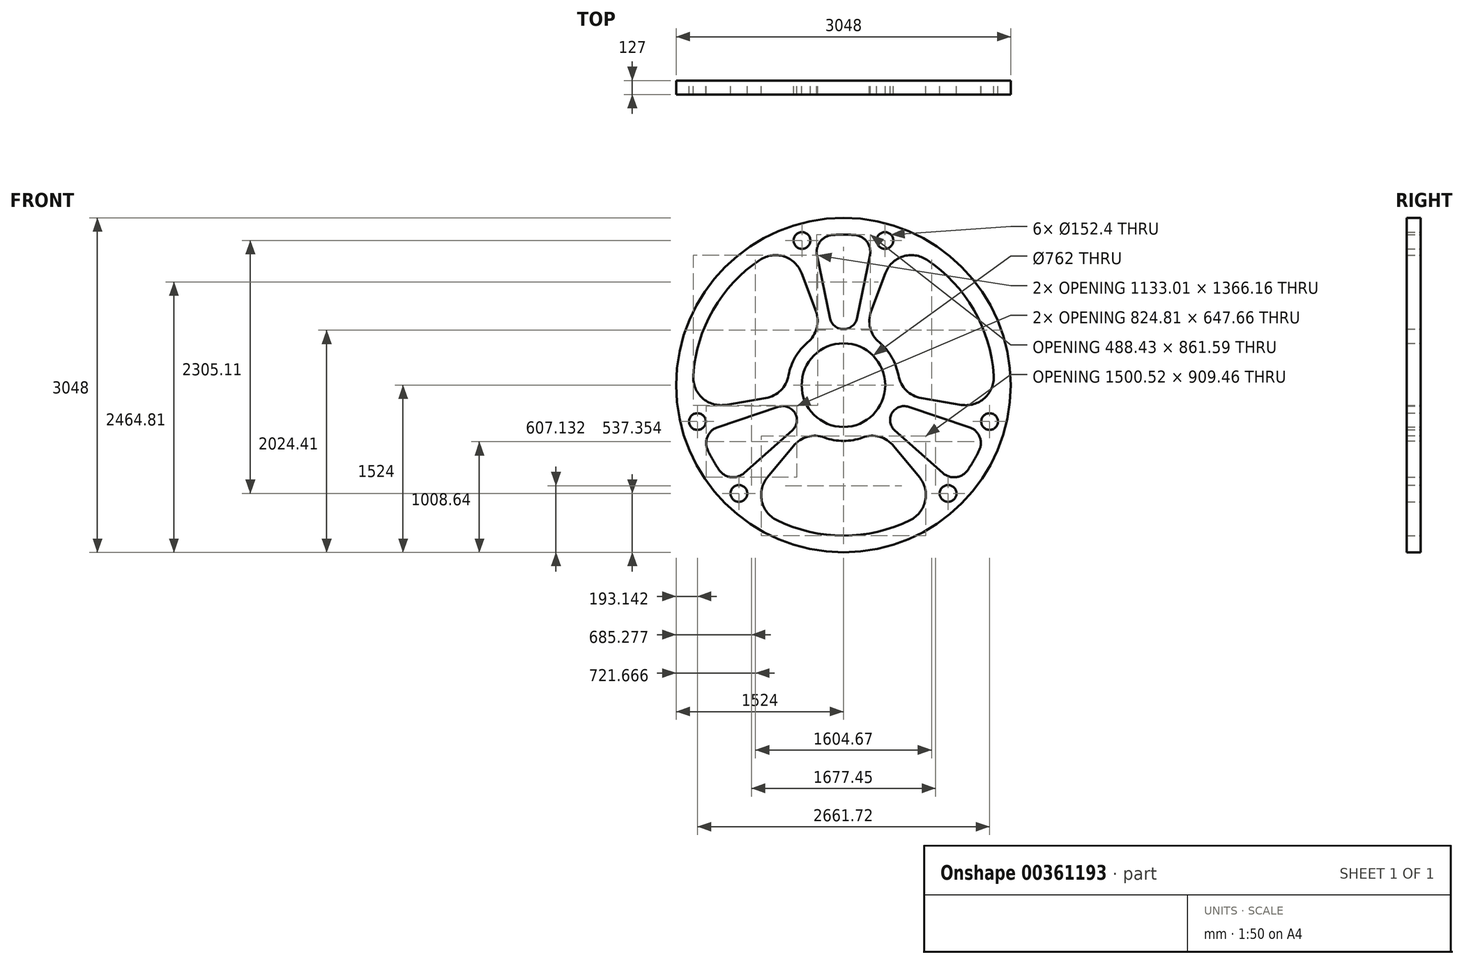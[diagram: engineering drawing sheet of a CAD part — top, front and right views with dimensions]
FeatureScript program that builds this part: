
annotation { "Feature Type Name" : "Feature", "Feature Type Description" : "" }
export const myFeature = defineFeature(function(context is Context, id is Id, definition is map)
    precondition{}
    {
        {
            var Q0;
            Q0=qCreatedBy(makeId("Front.planeOp"),FACE);
            var sketch = newSketch(context, id + "F0", { "sketchPlane" : qUnion([Q0])});
            skCircle(sketch, "E0", {"center": v(0, 0) * mm, "radius": 1524 * mm});
            skLineSegment(sketch, "E1", {"start": v(-124.45, 611.7) * mm, "end": v(-241.16, 1185.35) * mm});
            skLineSegment(sketch, "E2", {"start": v(124.45, 611.7) * mm, "end": v(241.16, 1185.35) * mm});
            skArc(sketch, "E3", {"start": v(-103.3, 1367.7) * mm, "mid": v(-213.39, 1307.65) * mm, "end": v(-241.16, 1185.35) * mm});
            skArc(sketch, "E4", {"start": v(241.16, 1185.35) * mm, "mid": v(213.39, 1307.65) * mm, "end": v(103.3, 1367.7) * mm});
            skArc(sketch, "E5.trimOffspring", {"start": v(103.3, 1367.7) * mm, "mid": v(0, 1371.6) * mm, "end": v(-103.3, 1367.7) * mm});
            skArc(sketch, "E6", {"start": v(-124.45, 611.7) * mm, "mid": v(0, 510.01) * mm, "end": v(124.45, 611.7) * mm});
            skLineSegment(sketch, "E7", {"start": v(0, 508) * mm, "end": v(0, 510.01) * mm});
            skCircle(sketch, "E8", {"center": v(-378.06, 1318.47) * mm, "radius": 76.2 * mm});
            skCircle(sketch, "E9", {"center": v(378.06, 1318.47) * mm, "radius": 76.2 * mm});
            skPoint(sketch, "E10.endSnap0", {"position": v(0, -1371.6) * mm});
            skLineSegment(sketch, "E11", {"start": v(-456.97, -554.35) * mm, "end": v(-692.28, -839.8) * mm});
            skArc(sketch, "E12", {"start": v(-326.34, 389.31) * mm, "mid": v(-439.94, 254) * mm, "end": v(-500.33, 87.96) * mm});
            skArc(sketch, "E13", {"start": v(-692.28, -839.8) * mm, "mid": v(-744.67, -1054.47) * mm, "end": v(-609.08, -1228.95) * mm});
            skArc(sketch, "E14", {"start": v(456.97, -554.35) * mm, "mid": v(327.73, -470.84) * mm, "end": v(173.99, -477.28) * mm});
            skArc(sketch, "E15", {"start": v(-173.99, -477.28) * mm, "mid": v(-327.73, -470.84) * mm, "end": v(-456.97, -554.35) * mm});
            skArc(sketch, "E16.trimOffspring", {"start": v(-609.08, -1228.95) * mm, "mid": v(0, -1371.6) * mm, "end": v(609.08, -1228.95) * mm});
            skPoint(sketch, "E17.orphan", {"position": v(0, -1524) * mm});
            skArc(sketch, "E18", {"start": v(609.08, -1228.95) * mm, "mid": v(744.67, -1054.47) * mm, "end": v(692.28, -839.8) * mm});
            skLineSegment(sketch, "E19.trimOffspring", {"start": v(456.97, -554.35) * mm, "end": v(692.28, -839.8) * mm});
            skCircle(sketch, "E20", {"center": v(0, 0) * mm, "radius": 381 * mm});
            skArc(sketch, "E21", {"start": v(-759.76, 1141.95) * mm, "mid": v(-1187.84, 685.8) * mm, "end": v(-1368.84, 87) * mm});
            skCircle(sketch, "E22.1.0", {"center": v(-1330.86, -331.82) * mm, "radius": 76.2 * mm});
            skCircle(sketch, "E22.1.1", {"center": v(-952.8, -986.65) * mm, "radius": 76.2 * mm});
            skLineSegment(sketch, "E22.1.2", {"start": v(-591.97, -198.07) * mm, "end": v(-1147.13, -383.82) * mm});
            skArc(sketch, "E22.1.3", {"start": v(-1147.13, -383.82) * mm, "mid": v(-1239.15, -469.02) * mm, "end": v(-1236.12, -594.4) * mm});
            skArc(sketch, "E22.1.4", {"start": v(-1132.82, -773.31) * mm, "mid": v(-1025.76, -838.62) * mm, "end": v(-905.96, -801.53) * mm});
            skLineSegment(sketch, "E22.1.5", {"start": v(-467.52, -413.62) * mm, "end": v(-905.96, -801.53) * mm});
            skArc(sketch, "E22.1.6", {"start": v(-467.52, -413.62) * mm, "mid": v(-441.68, -255) * mm, "end": v(-591.97, -198.07) * mm});
            skCircle(sketch, "E22.2.0", {"center": v(952.8, -986.65) * mm, "radius": 76.2 * mm});
            skCircle(sketch, "E22.2.1", {"center": v(1330.86, -331.82) * mm, "radius": 76.2 * mm});
            skLineSegment(sketch, "E22.2.2", {"start": v(467.52, -413.62) * mm, "end": v(905.96, -801.53) * mm});
            skArc(sketch, "E22.2.3", {"start": v(905.96, -801.53) * mm, "mid": v(1025.76, -838.62) * mm, "end": v(1132.82, -773.31) * mm});
            skArc(sketch, "E22.2.4", {"start": v(1236.12, -594.4) * mm, "mid": v(1239.15, -469.02) * mm, "end": v(1147.13, -383.82) * mm});
            skLineSegment(sketch, "E22.2.5", {"start": v(591.97, -198.07) * mm, "end": v(1147.13, -383.82) * mm});
            skArc(sketch, "E22.2.6", {"start": v(591.97, -198.07) * mm, "mid": v(441.68, -255) * mm, "end": v(467.52, -413.62) * mm});
            skArc(sketch, "E23.1.0", {"start": v(500.33, 87.96) * mm, "mid": v(571.62, -48.4) * mm, "end": v(708.57, -118.57) * mm});
            skLineSegment(sketch, "E23.1.1", {"start": v(708.57, -118.57) * mm, "end": v(1073.43, -179.63) * mm});
            skArc(sketch, "E23.1.2", {"start": v(1073.43, -179.63) * mm, "mid": v(1285.53, -117.67) * mm, "end": v(1368.84, 87) * mm});
            skLineSegment(sketch, "E23.1.4", {"start": v(251.6, 672.92) * mm, "end": v(381.15, 1019.43) * mm});
            skArc(sketch, "E23.1.5", {"start": v(251.6, 672.92) * mm, "mid": v(243.9, 519.24) * mm, "end": v(326.34, 389.31) * mm});
            skArc(sketch, "E23.1.6", {"start": v(759.76, 1141.95) * mm, "mid": v(540.86, 1172.14) * mm, "end": v(381.15, 1019.43) * mm});
            skArc(sketch, "E23.2.0", {"start": v(-326.34, 389.31) * mm, "mid": v(-243.9, 519.24) * mm, "end": v(-251.6, 672.92) * mm});
            skLineSegment(sketch, "E23.2.1", {"start": v(-251.6, 672.92) * mm, "end": v(-381.15, 1019.43) * mm});
            skArc(sketch, "E23.2.2", {"start": v(-381.15, 1019.43) * mm, "mid": v(-540.86, 1172.14) * mm, "end": v(-759.76, 1141.95) * mm});
            skLineSegment(sketch, "E23.2.4", {"start": v(-708.57, -118.57) * mm, "end": v(-1073.43, -179.63) * mm});
            skArc(sketch, "E23.2.5", {"start": v(-708.57, -118.57) * mm, "mid": v(-571.62, -48.4) * mm, "end": v(-500.33, 87.96) * mm});
            skArc(sketch, "E23.2.6", {"start": v(-1368.84, 87) * mm, "mid": v(-1285.53, -117.67) * mm, "end": v(-1073.43, -179.63) * mm});
            skArc(sketch, "E24.trimOffspring", {"start": v(-173.99, -477.28) * mm, "mid": v(0, -508) * mm, "end": v(173.99, -477.28) * mm});
            skArc(sketch, "E25.trimOffspring", {"start": v(500.33, 87.96) * mm, "mid": v(439.94, 254) * mm, "end": v(326.34, 389.31) * mm});
            skArc(sketch, "E26.trimOffspring", {"start": v(1132.82, -773.31) * mm, "mid": v(1187.84, -685.8) * mm, "end": v(1236.12, -594.4) * mm});
            skArc(sketch, "E27.trimOffspring", {"start": v(-609.08, -1228.95) * mm, "mid": v(-312.78, -1335.46) * mm, "end": v(0, -1371.6) * mm});
            skArc(sketch, "E28.trimOffspring", {"start": v(-1236.12, -594.4) * mm, "mid": v(-1187.84, -685.8) * mm, "end": v(-1132.82, -773.31) * mm});
            skArc(sketch, "E29.trimOffspring", {"start": v(1368.84, 87) * mm, "mid": v(1187.84, 685.8) * mm, "end": v(759.76, 1141.95) * mm});
            skCircle(sketch, "E30", {"center": v(0, 0) * mm, "radius": 127 * mm});
            skCircle(sketch, "E31", {"center": v(0, 254.8) * mm, "radius": 50.8 * mm});
            skCircle(sketch, "E32.1.0", {"center": v(220.67, -127.4) * mm, "radius": 50.8 * mm});
            skCircle(sketch, "E32.2.0", {"center": v(-220.67, -127.4) * mm, "radius": 50.8 * mm});
            skLineSegment(sketch, "E32.anchor1", {"start": v(0, 0) * mm, "end": v(0, 254.8) * mm, "construction": true});
            skLineSegment(sketch, "E32.anchor2", {"start": v(0, 0) * mm, "end": v(-220.67, -127.4) * mm, "construction": true});
            skCircle(sketch, "E33", {"center": v(0, -254.8) * mm, "radius": 50.8 * mm});
            skCircle(sketch, "E34.1.0", {"center": v(220.67, 127.4) * mm, "radius": 50.8 * mm});
            skCircle(sketch, "E34.2.0", {"center": v(-220.67, 127.4) * mm, "radius": 50.8 * mm});
            skLineSegment(sketch, "E35", {"start": v(0, 0) * mm, "end": v(0, 127) * mm});
            skLineSegment(sketch, "E36", {"start": v(0, 127) * mm, "end": v(0, -127) * mm});
            skArc(sketch, "E37", {"start": v(-25.27, -124.46) * mm, "mid": v(0, -152.4) * mm, "end": v(25.27, -124.46) * mm});
            skLineSegment(sketch, "E38", {"start": v(0, 0) * mm, "end": v(127, 0) * mm});
            skLineSegment(sketch, "E39", {"start": v(127, 0) * mm, "end": v(-127, 0) * mm});
            skArc(sketch, "E40", {"start": v(124.46, -25.27) * mm, "mid": v(152.4, 0) * mm, "end": v(124.46, 25.27) * mm});
            skArc(sketch, "E41", {"start": v(-124.46, 25.27) * mm, "mid": v(-152.4, 0) * mm, "end": v(-124.46, -25.27) * mm});
            skArc(sketch, "E42", {"start": v(25.27, 124.46) * mm, "mid": v(0, 152.4) * mm, "end": v(-25.27, 124.46) * mm});
            skSolve(sketch);
        }
        {
            var Q0;
            Q0 = qSketchRegion(id + "F0", true);
            extrude(context, id + "F1", {"entities" : qUnion([Q0]), "depth" : 127 * mm});
        }
    });
